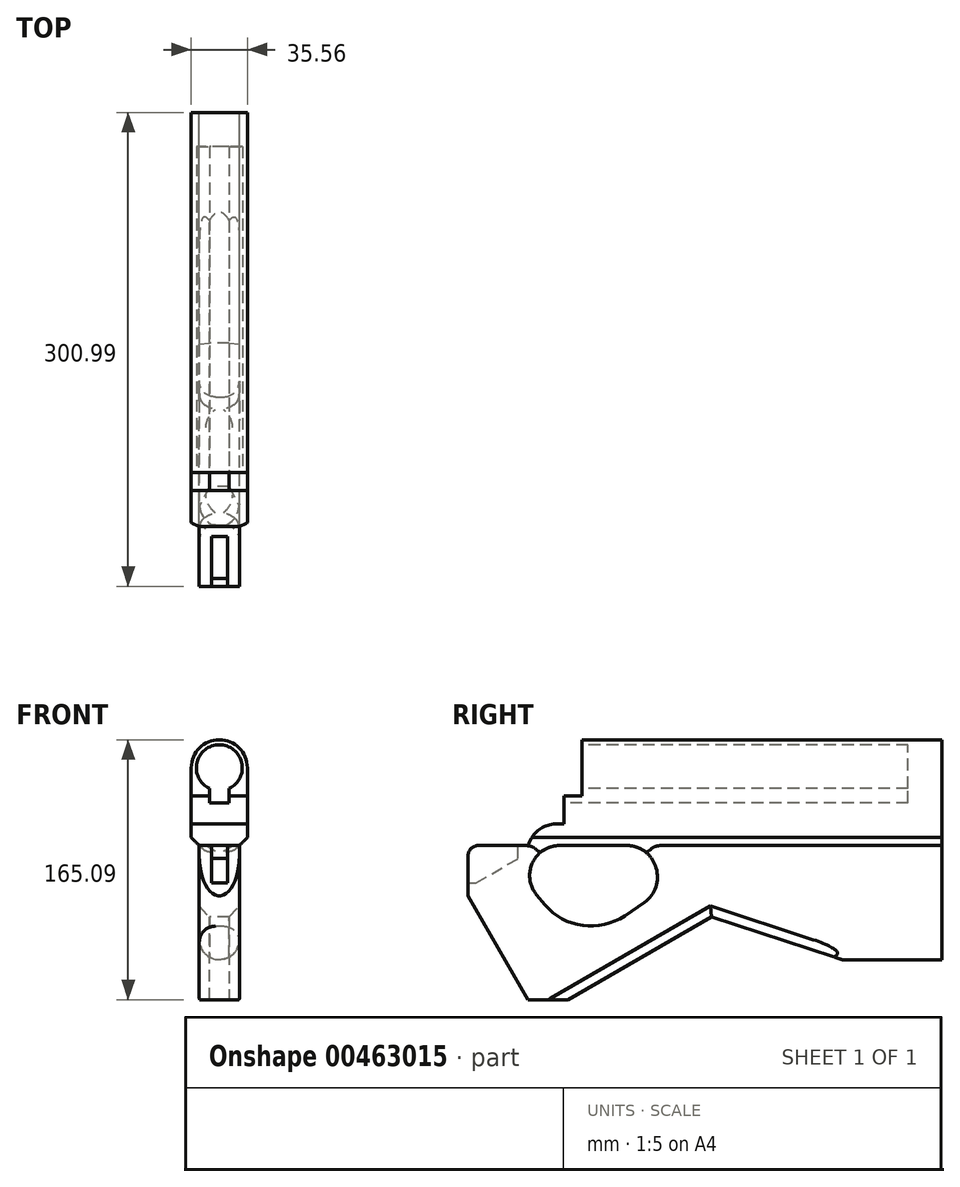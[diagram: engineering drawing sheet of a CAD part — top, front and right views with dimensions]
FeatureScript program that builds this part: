
annotation { "Feature Type Name" : "Feature", "Feature Type Description" : "" }
export const myFeature = defineFeature(function(context is Context, id is Id, definition is map)
    precondition{}
    {
        {
            var Q0;
            Q0=qCreatedBy(makeId("Front.planeOp"),FACE);
            var sketch = newSketch(context, id + "F0", { "sketchPlane" : qUnion([Q0])});
            skLineSegment(sketch, "E0", {"start": v(0, 0) * mm, "end": v(-11.43, 0) * mm});
            skLineSegment(sketch, "E1", {"start": v(-11.43, 0) * mm, "end": v(-11.43, -31.75) * mm});
            skLineSegment(sketch, "E2", {"start": v(-11.43, -31.75) * mm, "end": v(0, -31.75) * mm});
            skLineSegment(sketch, "E3", {"start": v(0, -31.75) * mm, "end": v(0, 0) * mm});
            skLineSegment(sketch, "E4", {"start": v(0, 0) * mm, "end": v(11.43, 0) * mm});
            skLineSegment(sketch, "E5", {"start": v(11.43, 0) * mm, "end": v(11.43, -31.75) * mm});
            skLineSegment(sketch, "E6", {"start": v(11.43, -31.75) * mm, "end": v(0, -31.75) * mm});
            skLineSegment(sketch, "E7", {"start": v(0, 0) * mm, "end": v(0, 49.4) * mm, "construction": true});
            skArc(sketch, "E8", {"start": v(17.78, 49.4) * mm, "mid": v(0, 67.18) * mm, "end": v(-17.78, 49.4) * mm});
            skLineSegment(sketch, "E9", {"start": v(17.78, 49.4) * mm, "end": v(11.43, 0) * mm});
            skLineSegment(sketch, "E10", {"start": v(-17.78, 49.4) * mm, "end": v(-11.43, 0) * mm});
            skArc(sketch, "E11", {"start": v(6.35, 36.25) * mm, "mid": v(0, 64) * mm, "end": v(-6.35, 36.25) * mm});
            skLineSegment(sketch, "E12", {"start": v(-17.78, 49.4) * mm, "end": v(17.78, 49.4) * mm, "construction": true});
            skLineSegment(sketch, "E13", {"start": v(0, 27.18) * mm, "end": v(6.35, 27.18) * mm});
            skLineSegment(sketch, "E14", {"start": v(0, 27.18) * mm, "end": v(-6.35, 27.18) * mm});
            skLineSegment(sketch, "E15", {"start": v(-6.35, 27.18) * mm, "end": v(-6.35, 36.25) * mm});
            skLineSegment(sketch, "E16", {"start": v(6.35, 27.18) * mm, "end": v(6.35, 36.25) * mm});
            skSolve(sketch);
        }
        {
            var Q0;
            Q0=qCreatedBy(makeId("Right.planeOp"),FACE);
            var sketch = newSketch(context, id + "F1", { "sketchPlane" : qUnion([Q0])});
            skLineSegment(sketch, "E17", {"start": v(0, 0) * mm, "end": v(38.1, 0) * mm});
            skLineSegment(sketch, "E18", {"start": v(0, 0) * mm, "end": v(0, -31.92) * mm});
            skLineSegment(sketch, "E19", {"start": v(0, -31.92) * mm, "end": v(44.45, -108.91) * mm});
            skLineSegment(sketch, "E20", {"start": v(154.44, -45.41) * mm, "end": v(237.5, -72.52) * mm});
            skLineSegment(sketch, "E21", {"start": v(237.5, -72.52) * mm, "end": v(301, -72.52) * mm});
            skLineSegment(sketch, "E22", {"start": v(301, -72.52) * mm, "end": v(301, 67.18) * mm});
            skLineSegment(sketch, "E23", {"start": v(301, 67.18) * mm, "end": v(72.39, 67.18) * mm});
            skLineSegment(sketch, "E24", {"start": v(0, 49.4) * mm, "end": v(301, 49.4) * mm, "construction": true});
            skLineSegment(sketch, "E25", {"start": v(72.39, 67.18) * mm, "end": v(72.39, 49.4) * mm});
            skLineSegment(sketch, "E26", {"start": v(72.39, 49.4) * mm, "end": v(72.39, 31.62) * mm});
            skLineSegment(sketch, "E27", {"start": v(72.39, 31.62) * mm, "end": v(60.96, 31.62) * mm});
            skLineSegment(sketch, "E28", {"start": v(60.96, 31.62) * mm, "end": v(60.96, 13.84) * mm});
            skLineSegment(sketch, "E29", {"start": v(60.96, 13.84) * mm, "end": v(56.42, 13.84) * mm});
            skArc(sketch, "E30", {"start": v(56.42, 13.84) * mm, "mid": v(44.94, 10) * mm, "end": v(38.1, 0) * mm});
            skLineSegment(sketch, "E31", {"start": v(44.45, -108.91) * mm, "end": v(154.44, -45.41) * mm});
            skLineSegment(sketch, "E32", {"start": v(38.1, 0) * mm, "end": v(301, 0) * mm});
            skLineSegment(sketch, "E33", {"start": v(0, -23.62) * mm, "end": v(5.08, -23.62) * mm});
            skLineSegment(sketch, "E34", {"start": v(5.08, -23.62) * mm, "end": v(31.75, -8.26) * mm});
            skLineSegment(sketch, "E35", {"start": v(31.75, -8.26) * mm, "end": v(31.75, 0) * mm});
            skLineSegment(sketch, "E36", {"start": v(38.1, -97.91) * mm, "end": v(63.5, -97.91) * mm});
            skSolve(sketch);
        }
        {
            var Q0;
            {var subQ0=sQuery(id+"F1.wireOp",EDGE,"E33");Q0=makeQuery(id+"F1.imprint","IMPRINT",FACE,{"disambiguationData":[TD([[makeQuery(id+"F1.imprint","IMPRINT",EDGE,{"derivedFrom":subQ0}),1.0]])]});}
            var Q1;
            {var subQ5=sQuery(id+"F1.wireOp",EDGE,"E20");Q1=makeQuery(id+"F1.imprint","IMPRINT",FACE,{"disambiguationData":[TD([[makeQuery(id+"F1.imprint","IMPRINT",EDGE,{"derivedFrom":subQ5}),1.0]])]});}
            extrude(context, id + "F2", {"entities" : qUnion([Q0, Q1]), "endBound" : BoundingType.SYMMETRIC, "depth" : 25.4 * mm});
        }
        {
            var Q0;
            {var subQ0=sQuery(id+"F1.wireOp",EDGE,"E33");Q0=makeQuery(id+"F1.imprint","IMPRINT",FACE,{"disambiguationData":[TD([[makeQuery(id+"F1.imprint","IMPRINT",EDGE,{"derivedFrom":subQ0}),1.0]])]});}
            extrude(context, id + "F3", {"entities" : qUnion([Q0]), "operationType" : NewBodyOperationType.REMOVE, "endBound" : BoundingType.SYMMETRIC, "oppositeDirection" : true, "depth" : 10.16 * mm});
        }
        {
            var Q0;
            {var subQ0=sQuery(id+"F1.wireOp",EDGE,"E23");Q0=makeQuery(id+"F1.imprint","IMPRINT",FACE,{"disambiguationData":[TD([[makeQuery(id+"F1.imprint","IMPRINT",EDGE,{"derivedFrom":subQ0}),1.0]])]});}
            extrude(context, id + "F4", {"entities" : qUnion([Q0]), "operationType" : NewBodyOperationType.ADD, "endBound" : BoundingType.SYMMETRIC, "depth" : 35.56 * mm});
        }
        {
            var Q0;
            Q0=makeQuery(id+"F2.opExtrude","CAP_EDGE",EDGE,{"disambiguationData":[OSD([sQuery(id+"F1.wireOp",EDGE,"E31")])],"isStart":true});
            var Q1;
            Q1=makeQuery(id+"F2.opExtrude","CAP_EDGE",EDGE,{"disambiguationData":[OSD([sQuery(id+"F1.wireOp",EDGE,"E20")])],"isStart":true});
            var Q2;
            Q2=makeQuery(id+"F2.opExtrude","CAP_EDGE",EDGE,{"disambiguationData":[OSD([sQuery(id+"F1.wireOp",EDGE,"E31")])],"isStart":false});
            var Q3;
            Q3=makeQuery(id+"F2.opExtrude","CAP_EDGE",EDGE,{"disambiguationData":[OSD([sQuery(id+"F1.wireOp",EDGE,"E20")])],"isStart":false});
            chamfer(context, id + "F5", {"entities" : qUnion([Q0, Q1, Q2, Q3]), "width" : 6.35 * mm, "tangentPropagation" : true});
        }
        {
            var Q0;
            Q0=makeQuery(id+"F2.opExtrude","CAP_EDGE",EDGE,{"disambiguationData":[OSD([sQuery(id+"F1.wireOp",EDGE,"E19")])],"isStart":true});
            var Q1;
            Q1=makeQuery(id+"F2.opExtrude","CAP_EDGE",EDGE,{"disambiguationData":[OSD([sQuery(id+"F1.wireOp",EDGE,"E19")])],"isStart":false});
            var Q2;
            Q2=makeQuery(id+"F2.opExtrude","CAP_EDGE",EDGE,{"disambiguationData":[OSD([sQuery(id+"F1.wireOp",EDGE,"E21")])],"isStart":false});
            var Q3;
            Q3=makeQuery(id+"F2.opExtrude","CAP_EDGE",EDGE,{"disambiguationData":[OSD([sQuery(id+"F1.wireOp",EDGE,"E21")])],"isStart":true});
            fillet(context, id + "F6", {"entities" : qUnion([Q0, Q1, Q2, Q3]), "radius" : 12.7 * mm, "tangentPropagation" : true, "allowEdgeOverflow" : false});
        }
        {
            var Q0;
            Q0=makeQuery(id+"F4.opExtrude","CAP_EDGE",EDGE,{"disambiguationData":[OSD([sQuery(id+"F1.wireOp",EDGE,"E23")])],"isStart":false});
            var Q1;
            Q1=makeQuery(id+"F4.opExtrude","CAP_EDGE",EDGE,{"disambiguationData":[OSD([sQuery(id+"F1.wireOp",EDGE,"E23")])],"isStart":true});
            fillet(context, id + "F7", {"entities" : qUnion([Q0, Q1]), "radius" : 17.78 * mm, "tangentPropagation" : true, "allowEdgeOverflow" : false});
        }
        {
            var Q0;
            Q0=makeQuery(id+"F0.imprint","IMPRINT",FACE,{"disambiguationData":[TD([[makeQuery(id+"F0.imprint","IMPRINT",EDGE,{"derivedFrom":sQuery(id+"F0.wireOp",EDGE,"E11")}),1.0]])]});
            extrude(context, id + "F8", {"entities" : qUnion([Q0]), "operationType" : NewBodyOperationType.REMOVE, "oppositeDirection" : true, "depth" : 279.4 * mm});
        }
        {
            var Q0;
            {var subQ1=sQuery(id+"F1.wireOp",EDGE,"E18");var subQ2=sQuery(id+"F1.wireOp",EDGE,"E17");Q0=makeQuery(id+"F3.boolean.opBoolean","SPLIT",EDGE,{"disambiguationData":[TD([makeQuery(id+"F3.opExtrude","CAP_FACE",FACE,{"disambiguationData":[OSD([subQ2,subQ1,sQuery(id+"F1.wireOp",EDGE,"E33"),sQuery(id+"F1.wireOp",EDGE,"E34"),sQuery(id+"F1.wireOp",EDGE,"E35")])],"isStart":true})])],"derivedFrom":makeQuery(id+"F2.opExtrude","SWEPT_EDGE",EDGE,{"disambiguationData":[OSD([subQ2,subQ1])]})});}
            var Q1;
            {var subQ1=sQuery(id+"F1.wireOp",EDGE,"E18");var subQ2=sQuery(id+"F1.wireOp",EDGE,"E17");Q1=makeQuery(id+"F3.boolean.opBoolean","SPLIT",EDGE,{"disambiguationData":[TD([makeQuery(id+"F3.opExtrude","CAP_FACE",FACE,{"disambiguationData":[OSD([subQ2,subQ1,sQuery(id+"F1.wireOp",EDGE,"E33"),sQuery(id+"F1.wireOp",EDGE,"E34"),sQuery(id+"F1.wireOp",EDGE,"E35")])],"isStart":false})])],"derivedFrom":makeQuery(id+"F2.opExtrude","SWEPT_EDGE",EDGE,{"disambiguationData":[OSD([subQ2,subQ1])]})});}
            fillet(context, id + "F9", {"entities" : qUnion([Q0, Q1]), "radius" : 6.35 * mm, "tangentPropagation" : true, "allowEdgeOverflow" : false});
        }
        {
            var Q0;
            Q0=makeQuery(id+"F4.opExtrude","CAP_EDGE",EDGE,{"disambiguationData":[OSD([sQuery(id+"F1.wireOp",EDGE,"E32")])],"isStart":false});
            var Q1;
            Q1=makeQuery(id+"F4.opExtrude","CAP_EDGE",EDGE,{"disambiguationData":[OSD([sQuery(id+"F1.wireOp",EDGE,"E32")])],"isStart":true});
            chamfer(context, id + "F10", {"entities" : qUnion([Q0, Q1]), "width" : 5.08 * mm, "tangentPropagation" : true});
        }
        {
            var Q0;
            Q0=qCreatedBy(makeId("Right.planeOp"),FACE);
            var sketch = newSketch(context, id + "F11", { "sketchPlane" : qUnion([Q0])});
            skLineSegment(sketch, "E37", {"start": v(58.08, 0) * mm, "end": v(100.83, 0) * mm});
            skLineSegment(sketch, "E38", {"start": v(118.92, -13.08) * mm, "end": v(119.31, -14.28) * mm});
            skLineSegment(sketch, "E39", {"start": v(111.98, -35.98) * mm, "end": v(99.45, -44.54) * mm});
            skLineSegment(sketch, "E40", {"start": v(43.48, -31.3) * mm, "end": v(48.76, -37.58) * mm});
            skPoint(sketch, "E41.visualSharp", {"position": v(17.22, 0) * mm});
            skArc(sketch, "E41.filletArc", {"start": v(58.08, 0) * mm, "mid": v(40.81, -11) * mm, "end": v(43.48, -31.3) * mm});
            skPoint(sketch, "E42.visualSharp", {"position": v(70.95, -64.03) * mm});
            skArc(sketch, "E42.filletArc", {"start": v(48.76, -37.58) * mm, "mid": v(72.76, -50.84) * mm, "end": v(99.45, -44.54) * mm});
            skPoint(sketch, "E43.visualSharp", {"position": v(114.6, 0) * mm});
            skArc(sketch, "E43.filletArc", {"start": v(118.92, -13.08) * mm, "mid": v(111.99, -3.61) * mm, "end": v(100.83, 0) * mm});
            skPoint(sketch, "E44.visualSharp", {"position": v(123.8, -27.9) * mm});
            skArc(sketch, "E44.filletArc", {"start": v(111.98, -35.98) * mm, "mid": v(119.27, -26.36) * mm, "end": v(119.31, -14.28) * mm});
            skSolve(sketch);
        }
        {
            var Q0;
            Q0=makeQuery(id+"F11.imprint","IMPRINT",FACE,{"disambiguationData":[TD([[makeQuery(id+"F11.imprint","IMPRINT",EDGE,{"derivedFrom":sQuery(id+"F11.wireOp",EDGE,"E37")}),-1.0]])]});
            extrude(context, id + "F12", {"entities" : qUnion([Q0]), "operationType" : NewBodyOperationType.REMOVE, "endBound" : BoundingType.SYMMETRIC, "oppositeDirection" : true, "depth" : 76.2 * mm});
        }
        {
            var Q0;
            Q0=makeQuery(id+"F12.boolean.opBoolean","INTERSECT",EDGE,{"derivedFrom":[makeQuery(id+"F2.opExtrude","CAP_FACE",FACE,{"disambiguationData":[OSD([sQuery(id+"F1.wireOp",EDGE,"E17"),sQuery(id+"F1.wireOp",EDGE,"E18"),sQuery(id+"F1.wireOp",EDGE,"E19"),sQuery(id+"F1.wireOp",EDGE,"E20"),sQuery(id+"F1.wireOp",EDGE,"E21"),sQuery(id+"F1.wireOp",EDGE,"E22"),sQuery(id+"F1.wireOp",EDGE,"E31"),sQuery(id+"F1.wireOp",EDGE,"E32")])],"isStart":false}),makeQuery(id+"F12.opExtrude","SWEPT_FACE",FACE,{"disambiguationData":[OSD([sQuery(id+"F11.wireOp",EDGE,"E40")])]})]});
            var Q1;
            Q1=makeQuery(id+"F12.boolean.opBoolean","INTERSECT",EDGE,{"derivedFrom":[makeQuery(id+"F2.opExtrude","CAP_FACE",FACE,{"disambiguationData":[OSD([sQuery(id+"F1.wireOp",EDGE,"E17"),sQuery(id+"F1.wireOp",EDGE,"E18"),sQuery(id+"F1.wireOp",EDGE,"E19"),sQuery(id+"F1.wireOp",EDGE,"E20"),sQuery(id+"F1.wireOp",EDGE,"E21"),sQuery(id+"F1.wireOp",EDGE,"E22"),sQuery(id+"F1.wireOp",EDGE,"E31"),sQuery(id+"F1.wireOp",EDGE,"E32")])],"isStart":true}),makeQuery(id+"F12.opExtrude","SWEPT_FACE",FACE,{"disambiguationData":[OSD([sQuery(id+"F11.wireOp",EDGE,"E40")])]})]});
            fillet(context, id + "F13", {"entities" : qUnion([Q0, Q1]), "radius" : 10.16 * mm, "tangentPropagation" : true, "allowEdgeOverflow" : false});
        }
    });
